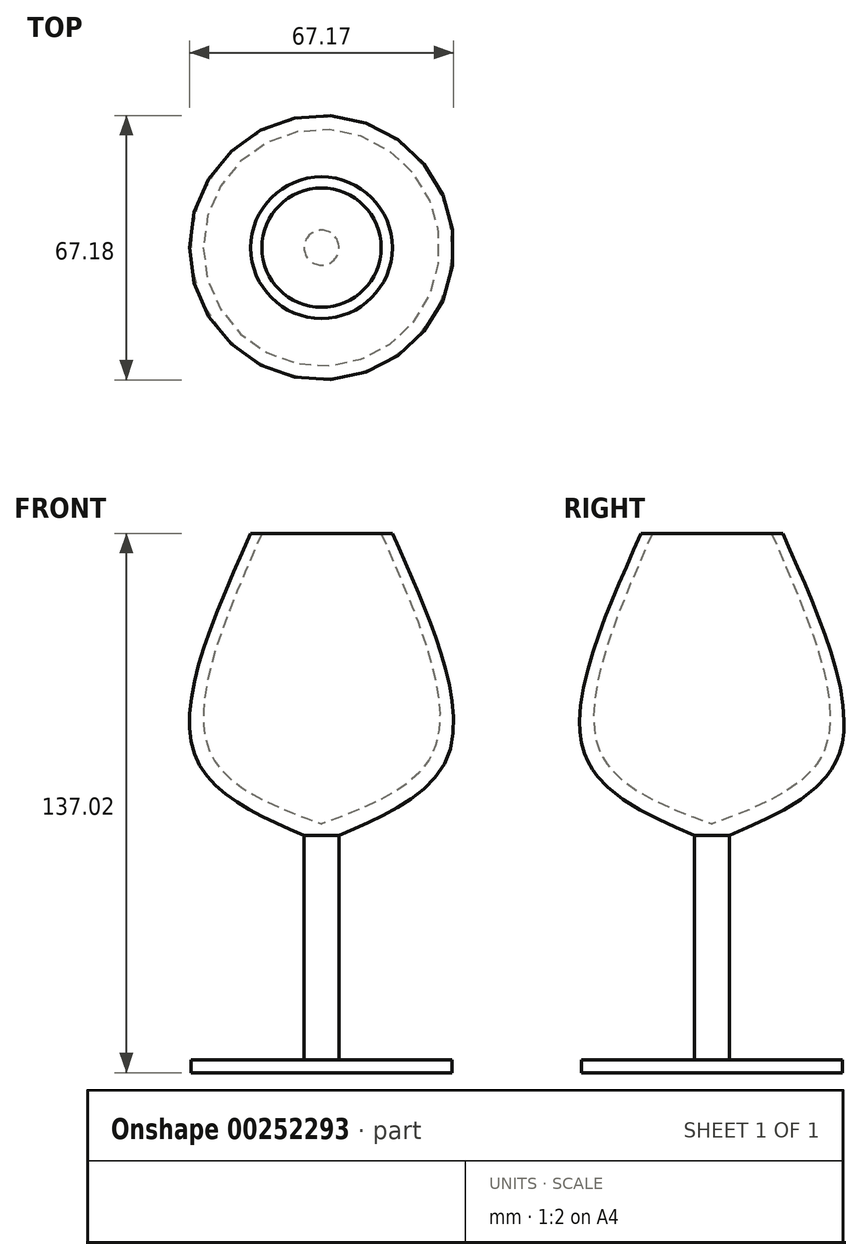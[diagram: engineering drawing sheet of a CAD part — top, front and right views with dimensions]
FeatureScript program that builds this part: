
annotation { "Feature Type Name" : "Feature", "Feature Type Description" : "" }
export const myFeature = defineFeature(function(context is Context, id is Id, definition is map)
    precondition{}
    {
        {
            var Q0;
            Q0=qCreatedBy(makeId("Front.planeOp"),FACE);
            var sketch = newSketch(context, id + "F0", { "sketchPlane" : qUnion([Q0])});
            skLineSegment(sketch, "E0", {"start": v(0, -86.46) * mm, "end": v(0, 85.28) * mm, "construction": true});
            skLineSegment(sketch, "E1", {"start": v(0, -76.15) * mm, "end": v(-33.19, -76.15) * mm});
            skLineSegment(sketch, "E2", {"start": v(-33.19, -76.15) * mm, "end": v(-33.19, -72.9) * mm});
            skLineSegment(sketch, "E3", {"start": v(-33.19, -72.9) * mm, "end": v(-4.43, -72.9) * mm});
            skFitSpline(sketch, "E4", {"points": [v(-4.43, -72.9) * mm, v(-4.43, -15.92) * mm], "startDerivative": vector(0, 56.98) * mm, "endDerivative": vector(0, 56.98) * mm});
            skFitSpline(sketch, "E5", {"points": [v(-4.43, -15.92) * mm, v(-32.37, 4.97) * mm, v(-18, 60.87) * mm], "startDerivative": vector(-83.45, 36.48) * mm, "endDerivative": vector(50.72, 113.86) * mm});
            skLineSegment(sketch, "E6", {"start": v(0, 60.87) * mm, "end": v(0, -76.15) * mm});
            skPoint(sketch, "E7.1.internal.orphan", {"position": v(0, 60.87) * mm});
            skLineSegment(sketch, "E8", {"start": v(-18, 60.87) * mm, "end": v(-15.15, 60.87) * mm});
            skFitSpline(sketch, "E9", {"points": [v(-15.15, 60.87) * mm, v(-28.7, 6.08) * mm, v(0, -12.97) * mm], "startDerivative": vector(-49.27, -112.78) * mm, "endDerivative": vector(85.07, -31.57) * mm});
            skSolve(sketch);
        }
        {
            var Q0;
            {var subQ0=sQuery(id+"F0.wireOp",EDGE,"E1");Q0=makeQuery(id+"F0.imprint","IMPRINT",FACE,{"disambiguationData":[TD([[makeQuery(id+"F0.imprint","IMPRINT",EDGE,{"derivedFrom":subQ0}),-1.0]])]});}
            var Q1;
            Q1=sQuery(id+"F0.wireOp",EDGE,"E0");
            revolve(context, id + "F1", {"entities" : qUnion([Q0]), "axis" : qUnion([Q1]), "revolveType" : RevolveType.FULL});
        }
    });
